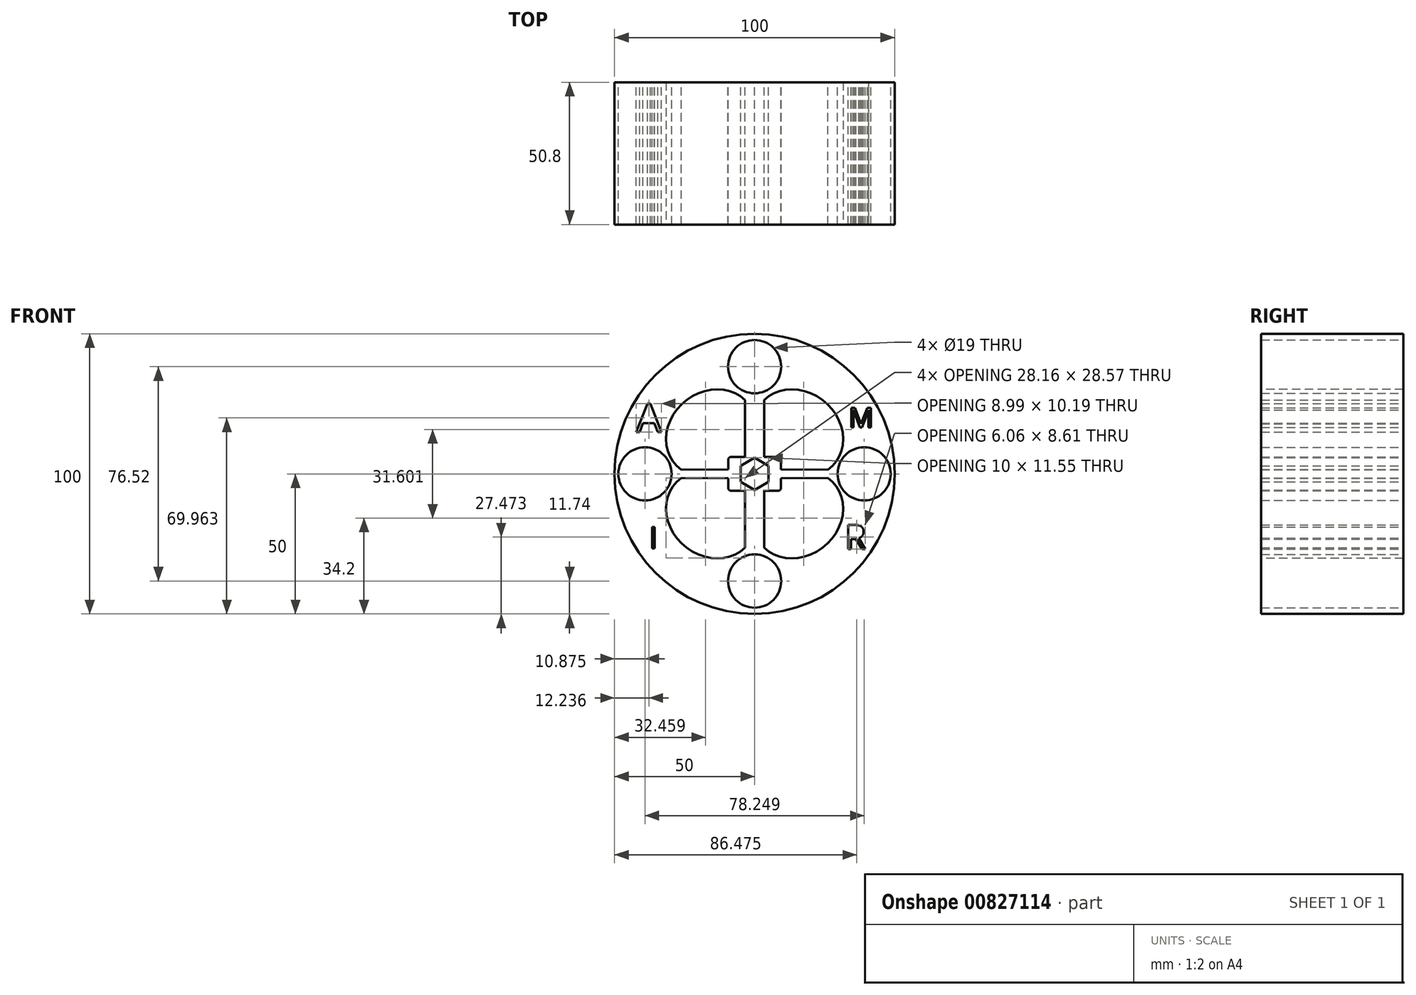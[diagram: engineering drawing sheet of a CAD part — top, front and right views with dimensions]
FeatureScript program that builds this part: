
annotation { "Feature Type Name" : "Feature", "Feature Type Description" : "" }
export const myFeature = defineFeature(function(context is Context, id is Id, definition is map)
    precondition{}
    {
        {
            var Q0;
            Q0=qCreatedBy(makeId("Front.planeOp"),FACE);
            var sketch = newSketch(context, id + "F0", { "sketchPlane" : qUnion([Q0])});
            skCircle(sketch, "E0", {"center": v(0, 0) * mm, "radius": 50 * mm});
            skCircle(sketch, "E1.cCircle", {"center": v(0, 0) * mm, "radius": 5 * mm, "construction": true});
            skLineSegment(sketch, "E1.0", {"start": v(5, 2.89) * mm, "end": v(5, -2.89) * mm});
            skLineSegment(sketch, "E1.1", {"start": v(5, -2.89) * mm, "end": v(0, -5.77) * mm});
            skLineSegment(sketch, "E1.2", {"start": v(0, -5.77) * mm, "end": v(-5, -2.89) * mm});
            skLineSegment(sketch, "E1.3", {"start": v(-5, -2.89) * mm, "end": v(-5, 2.89) * mm});
            skLineSegment(sketch, "E1.4", {"start": v(-5, 2.89) * mm, "end": v(0, 5.77) * mm});
            skLineSegment(sketch, "E1.5", {"start": v(0, 5.77) * mm, "end": v(5, 2.89) * mm});
            skPoint(sketch, "E1.0.midPoint", {"position": v(5, 0) * mm});
            skCircle(sketch, "E2", {"center": v(0, 38.26) * mm, "radius": 9.5 * mm});
            skCircle(sketch, "E3.MirrorC", {"center": v(0, -38.26) * mm, "radius": 9.5 * mm});
            skPoint(sketch, "E4.endSnap0", {"position": v(-2.5, 4.33) * mm});
            skPoint(sketch, "E4.end.orphan", {"position": v(-2.5, 10.03) * mm});
            skPoint(sketch, "E5.start.orphan", {"position": v(-9.3, 5.77) * mm});
            skPoint(sketch, "E6.end.orphan", {"position": v(25.63, -3.36) * mm});
            skPoint(sketch, "E7.end.orphan", {"position": v(25.63, 2.07) * mm});
            skPoint(sketch, "E8.start.orphan", {"position": v(22.77, 2.07) * mm});
            skPoint(sketch, "E9.center.orphan", {"position": v(-36.45, 0) * mm});
            skCircle(sketch, "E10", {"center": v(39.12, 0) * mm, "radius": 9.5 * mm});
            skCircle(sketch, "E11.MirrorC", {"center": v(-39.12, 0) * mm, "radius": 9.5 * mm});
            skLineSegment(sketch, "E12", {"start": v(3.1, 3.98) * mm, "end": v(3.1, 3.92) * mm});
            skPoint(sketch, "E13.visualSharp", {"position": v(-10.86, 1.24) * mm});
            skPoint(sketch, "E14.visualSharp", {"position": v(-9.45, -6.1) * mm});
            skPoint(sketch, "E15.end.orphan", {"position": v(-26.14, -1.58) * mm});
            skPoint(sketch, "E15.start.orphan", {"position": v(-10.86, -1.58) * mm});
            skPoint(sketch, "E16.MirrorCS.end.orphan", {"position": v(-2.5, -25.33) * mm});
            skPoint(sketch, "E16.MirrorCS.start.orphan", {"position": v(-2.5, -10.03) * mm});
            skPoint(sketch, "E17.start.orphan", {"position": v(-26.14, 1.24) * mm});
            skPoint(sketch, "E18.start.orphan", {"position": v(-9.3, 7.48) * mm});
            skPoint(sketch, "E19.start.orphan", {"position": v(-2.5, 25.33) * mm});
            skPoint(sketch, "E20.end.orphan", {"position": v(3.1, 25.33) * mm});
            skPoint(sketch, "E20.start.orphan", {"position": v(3.1, 10.03) * mm});
            skPoint(sketch, "E21.MirrorCS.end.orphan", {"position": v(26.14, 1.24) * mm});
            skPoint(sketch, "E21.MirrorCS.start.orphan", {"position": v(10.86, 1.24) * mm});
            skPoint(sketch, "E22.MirrorCS.end.orphan", {"position": v(26.14, -1.58) * mm});
            skPoint(sketch, "E22.MirrorCS.start.orphan", {"position": v(10.86, -1.58) * mm});
            skPoint(sketch, "E23.MirrorCS.end.orphan", {"position": v(3.1, -25.33) * mm});
            skPoint(sketch, "E23.MirrorCS.start.orphan", {"position": v(3.1, -10.03) * mm});
            skPoint(sketch, "E24.MirrorP", {"position": v(-9.45, 6.1) * mm});
            skEllipticalArc(sketch, "E25.MirrorCS", {});
            skLineSegment(sketch, "E26.MirrorCS", {"start": v(8.28, -6.1) * mm, "end": v(3.46, -6.1) * mm});
            skLineSegment(sketch, "E27.MirrorCS", {"start": v(3.46, -6.1) * mm, "end": v(3.46, -26.38) * mm});
            skArc(sketch, "E28.MirrorCS", {"start": v(9.45, -4.92) * mm, "mid": v(9.1, -5.75) * mm, "end": v(8.28, -6.1) * mm});
            skPoint(sketch, "E29.start.orphan", {"position": v(36.1, 26.5) * mm});
            skPoint(sketch, "E30.start.orphan", {"position": v(32.44, 26.5) * mm});
            skText(sketch, "E31", { "text": "R", "fontName": "OpenSans-Regular.ttf"});
            skText(sketch, "E32", { "text": "I\n", "fontName": "OpenSans-Regular.ttf"});
            skPoint(sketch, "E33.end.orphan", {"position": v(-37.17, 20.77) * mm});
            skPoint(sketch, "E34.start.orphan", {"position": v(-35.28, 32.47) * mm});
            skPoint(sketch, "E35.start.orphan", {"position": v(-33.74, 20.77) * mm});
            skPoint(sketch, "E36.start.orphan", {"position": v(-35.28, 28.38) * mm});
            skText(sketch, "E37", { "text": "A", "fontName": "OpenSans-Regular.ttf"});
            skPoint(sketch, "E38.end.orphan", {"position": v(35.99, 28.74) * mm});
            skPoint(sketch, "E39.start.orphan", {"position": v(37.71, 20.33) * mm});
            skPoint(sketch, "E40.end.orphan", {"position": v(32.44, 28.74) * mm});
            skPoint(sketch, "E41.start.orphan", {"position": v(31.03, 31.37) * mm});
            skPoint(sketch, "E42.start.orphan", {"position": v(35.38, 31.37) * mm});
            skPoint(sketch, "E43.end.orphan", {"position": v(31.03, 20.33) * mm});
            skPoint(sketch, "E43.start.orphan", {"position": v(32.44, 20.33) * mm});
            skText(sketch, "E44", { "text": "M", "fontName": "OpenSans-Regular.ttf"});
            skPoint(sketch, "E45.MirrorCS.end.orphan", {"position": v(-26.14, 1.58) * mm});
            skPoint(sketch, "E45.MirrorCS.start.orphan", {"position": v(-9.45, 1.12) * mm});
            skPoint(sketch, "E46.MirrorCS.end.orphan", {"position": v(-9.45, 4.92) * mm});
            skPoint(sketch, "E47.start.orphan", {"position": v(-9.45, -1.12) * mm});
            skPoint(sketch, "E48.MirrorCS.end.orphan", {"position": v(9.45, 4.92) * mm});
            skPoint(sketch, "E48.MirrorCS.start.orphan", {"position": v(9.45, 1.12) * mm});
            skPoint(sketch, "E49.MirrorCS.end.orphan", {"position": v(26.14, 1.58) * mm});
            skPoint(sketch, "E50.MirrorCS.end.orphan", {"position": v(9.45, -4.92) * mm});
            skPoint(sketch, "E50.MirrorCS.start.orphan", {"position": v(9.45, -1.12) * mm});
            skLineSegment(sketch, "E51", {"start": v(26.22, -1.51) * mm, "end": v(9.45, -1.58) * mm});
            skLineSegment(sketch, "E52", {"start": v(9.45, -1.58) * mm, "end": v(9.45, -4.92) * mm});
            skPoint(sketch, "E53.MirrorCS.end.orphan", {"position": v(3.46, 26.38) * mm});
            skPoint(sketch, "E53.MirrorCS.start.orphan", {"position": v(3.46, 6.1) * mm});
            skPoint(sketch, "E54.MirrorCS.start.orphan", {"position": v(8.28, 6.1) * mm});
            skPoint(sketch, "E55.end.orphan", {"position": v(9.45, 1.51) * mm});
            skPoint(sketch, "E56.MirrorCS.start.orphan", {"position": v(26.22, 1.51) * mm});
            skLineSegment(sketch, "E57.MirrorCS", {"start": v(26.22, 1.51) * mm, "end": v(9.45, 1.58) * mm});
            skEllipticalArc(sketch, "E58.MirrorCS", {});
            skLineSegment(sketch, "E59.MirrorCS", {"start": v(3.46, 6.1) * mm, "end": v(3.46, 26.38) * mm});
            skLineSegment(sketch, "E60.MirrorCS", {"start": v(8.28, 6.1) * mm, "end": v(3.46, 6.1) * mm});
            skLineSegment(sketch, "E61.MirrorCS", {"start": v(9.45, 1.58) * mm, "end": v(9.45, 4.92) * mm});
            skArc(sketch, "E62.MirrorCS", {"start": v(9.45, 4.92) * mm, "mid": v(9.1, 5.75) * mm, "end": v(8.28, 6.1) * mm});
            skPoint(sketch, "E63.MirrorCS.end.orphan", {"position": v(-3.46, 26.38) * mm});
            skPoint(sketch, "E63.MirrorCS.start.orphan", {"position": v(-3.46, 6.1) * mm});
            skPoint(sketch, "E64.MirrorCS.start.orphan", {"position": v(-8.28, 6.1) * mm});
            skPoint(sketch, "E65.end.orphan", {"position": v(-3.46, -26.38) * mm});
            skPoint(sketch, "E65.start.orphan", {"position": v(-3.46, -6.1) * mm});
            skPoint(sketch, "E66.start.orphan", {"position": v(-26.22, -1.51) * mm});
            skPoint(sketch, "E67.MirrorCS.end.orphan", {"position": v(-26.22, 1.51) * mm});
            skPoint(sketch, "E68.end.orphan", {"position": v(-9.45, -1.58) * mm});
            skPoint(sketch, "E14.filletArc.end.orphan", {"position": v(-8.28, -6.1) * mm});
            skPoint(sketch, "E14.filletArc.start.orphan", {"position": v(-9.45, -4.92) * mm});
            skLineSegment(sketch, "E69.MirrorCS", {"start": v(-3.46, 6.1) * mm, "end": v(-3.46, 26.38) * mm});
            skLineSegment(sketch, "E70.MirrorCS", {"start": v(-8.28, 6.1) * mm, "end": v(-3.46, 6.1) * mm});
            skLineSegment(sketch, "E71.MirrorCS", {"start": v(-9.45, 1.58) * mm, "end": v(-9.45, 4.92) * mm});
            skLineSegment(sketch, "E72.MirrorCS", {"start": v(-26.22, 1.51) * mm, "end": v(-9.45, 1.58) * mm});
            skEllipticalArc(sketch, "E73.MirrorCS", {});
            skLineSegment(sketch, "E74.MirrorCS", {"start": v(-26.22, -1.51) * mm, "end": v(-9.45, -1.58) * mm});
            skLineSegment(sketch, "E75.MirrorCS", {"start": v(-9.45, -1.58) * mm, "end": v(-9.45, -4.92) * mm});
            skEllipticalArc(sketch, "E76.MirrorCS", {});
            skLineSegment(sketch, "E77.MirrorCS", {"start": v(-3.46, -6.1) * mm, "end": v(-3.46, -26.38) * mm});
            skLineSegment(sketch, "E78.MirrorCS", {"start": v(-8.28, -6.1) * mm, "end": v(-3.46, -6.1) * mm});
            skArc(sketch, "E79.MirrorCS", {"start": v(-9.45, 4.92) * mm, "mid": v(-9.1, 5.75) * mm, "end": v(-8.28, 6.1) * mm});
            skArc(sketch, "E80.MirrorCS", {"start": v(-9.45, -4.92) * mm, "mid": v(-9.1, -5.75) * mm, "end": v(-8.28, -6.1) * mm});
            const initialGuessF0  = {"E25.MirrorCS": [0.015575654804706573, -0.014558497816324234, -0.7717082571345141, -0.6359767023015943, 0.01694377983366245, 0.014643182895431837, 0.09672092785218656, 3.3687528727316307], "E31": [0.03226, -0.02683, 1, 0, 0.00868], "E32": [-0.03768, -0.0266, 1, 0, 0.00773], "E37": [-0.04226, 0.01487, 1, 0, 0.01023], "E44": [0.03355, 0.01655, 1, 0, 0.00712], "E58.MirrorCS": [0.015575654804706573, 0.014558497816324234, -0.7717082571345141, 0.6359767023015943, 0.01694377983366245, 0.014643182895431837, 2.914432434447956, 6.1864643793274], "E73.MirrorCS": [-0.015575654804706573, 0.014558497816324234, 0.7717082571345141, 0.6359767023015943, 0.01694377983366245, 0.014643182895431837, 0.09672092785218656, 3.3687528727316303], "E76.MirrorCS": [-0.015575654804706573, -0.014558497816324234, 0.7717082571345141, -0.6359767023015943, 0.01694377983366245, 0.014643182895431837, 2.914432434447956, 6.1864643793274]};
            skSetInitialGuess(sketch, initialGuessF0);
            skSolve(sketch);
        }
        {
            var Q0;
            Q0=qSketchRegion(id+"F0",true);
            extrude(context, id + "F1", {"entities" : qUnion([Q0]), "depth" : 50.8 * mm, "offsetDistance" : 25.4 * mm});
        }
    });
